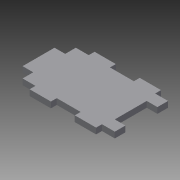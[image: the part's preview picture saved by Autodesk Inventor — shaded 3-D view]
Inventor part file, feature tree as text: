
AUTODESK INVENTOR PART (.ipt)
format: ipt  version: 2015 (Build 190159000, 159)  size: 102,912 bytes
history: native  units: mm
features: extrude x1, sketch x1
ambient origin geometry x8: Origin, YZ Plane, XZ Plane, XY Plane, X Axis, Y Axis, Z Axis, Center Point
bodies: Solid1 (feature_tree)
feature tree (2):
  extrude  "Extrusion1"  Depth=20.0mm
  sketch  "Sketch1"  dims[d2=5.5mm d3=20.0mm d4=5.5mm d5=20.0mm d6=90.0deg d8=30.0mm d11=10.0mm d12=10.0mm d13=30.0mm d14=10.0mm d15=90.0deg d16=5.5mm d17=0.0mm]
